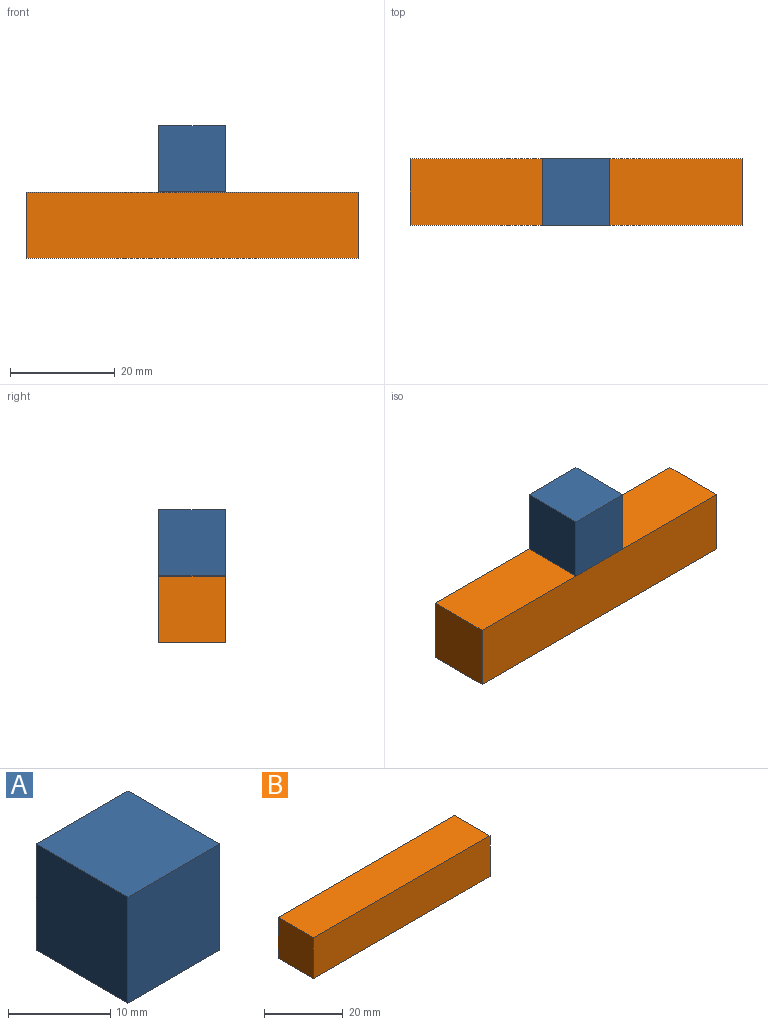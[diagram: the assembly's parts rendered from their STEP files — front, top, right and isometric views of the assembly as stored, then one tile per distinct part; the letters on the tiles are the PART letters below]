
ASSEMBLY  parts=2 mates=1
PART A: 6 faces, bbox 12.7x12.7x12.7 mm
  f0: plane 12.7x12.7mm, normal (0,0,-1), area 161.3mm2, adj f1,f3,f4,f5
  f1: plane 12.7x12.7mm, normal (1,0,0), area 161.3mm2, adj f0,f2,f4,f5
  f2: plane 12.7x12.7mm, normal (0,0,1), area 161.3mm2, adj f1,f3,f4,f5
  f3: plane 12.7x12.7mm, normal (-1,0,0), area 161.3mm2, adj f0,f2,f4,f5
  f4: plane 12.7x12.7mm, normal (0,-1,0), area 161.3mm2, adj f0,f1,f2,f3
  f5: plane 12.7x12.7mm, normal (0,1,0), area 161.3mm2, adj f0,f1,f2,f3
PART B: 6 faces, bbox 63.5x12.7x12.7 mm
  f0: plane 63.5x12.7mm, normal (0,0,-1), area 806.5mm2, adj f1,f3,f4,f5
  f1: plane 12.7x12.7mm, normal (1,0,0), area 161.3mm2, adj f0,f2,f4,f5
  f2: plane 63.5x12.7mm, normal (0,0,1), area 806.5mm2, adj f1,f3,f4,f5
  f3: plane 12.7x12.7mm, normal (-1,0,0), area 161.3mm2, adj f0,f2,f4,f5
  f4: plane 63.5x12.7mm, normal (0,-1,0), area 806.5mm2, adj f0,f1,f2,f3
  f5: plane 63.5x12.7mm, normal (0,1,0), area 806.5mm2, adj f0,f1,f2,f3
PLACE A rot(axis=(1,0,0),180deg) t=(17.75,-10.82,28.23)mm
PLACE B t=(21.05,1.88,30.56)mm
MATE slider A.f2 <-> B.f2  axis (0,0,-1) through (17.75,-4.47,-6.7)mm
